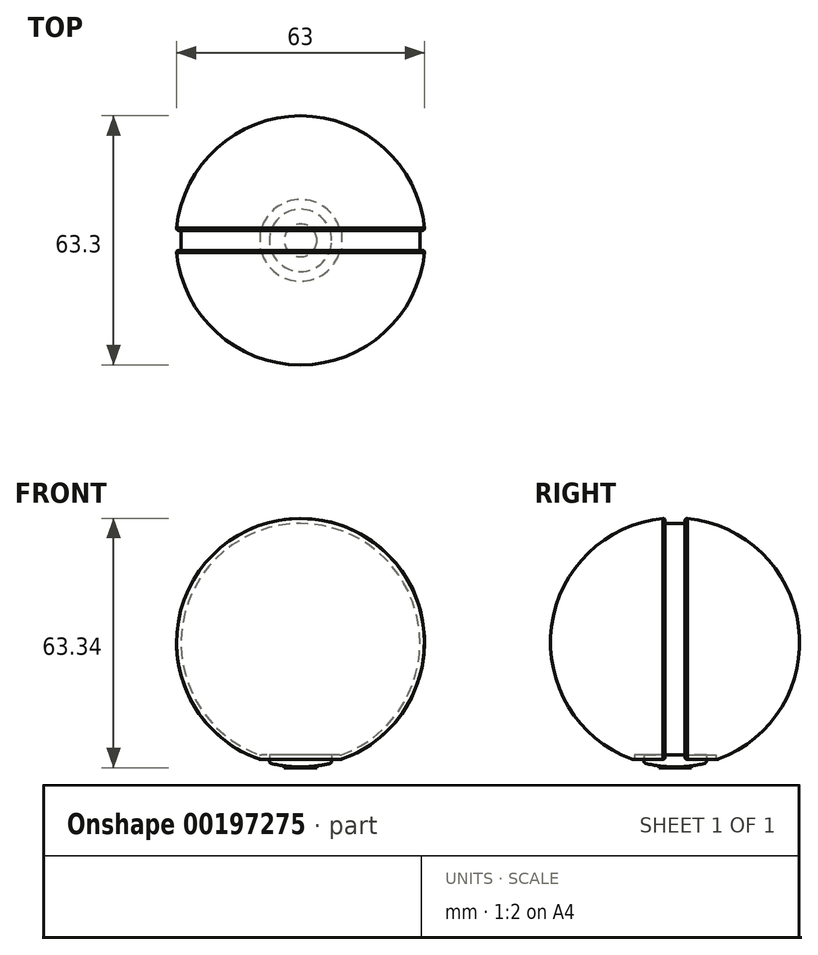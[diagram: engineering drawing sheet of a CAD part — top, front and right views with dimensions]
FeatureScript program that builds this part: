
annotation { "Feature Type Name" : "Feature", "Feature Type Description" : "" }
export const myFeature = defineFeature(function(context is Context, id is Id, definition is map)
    precondition{}
    {
        {
            var Q0;
            Q0=qCreatedBy(makeId("Front.planeOp"),FACE);
            var sketch = newSketch(context, id + "F0", { "sketchPlane" : qUnion([Q0])});
            skLineSegment(sketch, "E0", {"start": v(0, 0) * mm, "end": v(0, 63.3) * mm});
            skArc(sketch, "E1", {"start": v(0, 63.3) * mm, "mid": v(-31.65, 31.65) * mm, "end": v(0, 0) * mm});
            skSolve(sketch);
        }
        {
            var Q0;
            Q0=qSketchRegion(id+"F0",true);
            var Q1;
            Q1=sQuery(id+"F0.wireOp",EDGE,"E0");
            revolve(context, id + "F1", {"entities" : qUnion([Q0]), "axis" : qUnion([Q1]), "revolveType" : RevolveType.FULL});
        }
        {
            var Q0;
            Q0=qCreatedBy(makeId("Front.planeOp"),FACE);
            var sketch = newSketch(context, id + "F2", { "sketchPlane" : qUnion([Q0])});
            skLineSegment(sketch, "E2", {"start": v(10, -3.8) * mm, "end": v(10, 2.88) * mm});
            skLineSegment(sketch, "E3", {"start": v(-10, 2.88) * mm, "end": v(-10, -3.8) * mm});
            skLineSegment(sketch, "E4", {"start": v(0, 0) * mm, "end": v(0, 63.04) * mm, "construction": true});
            skArc(sketch, "E5", {"start": v(10, 2.88) * mm, "mid": v(0, 61.85) * mm, "end": v(-10, 2.88) * mm});
            skArc(sketch, "E6", {"start": v(10, -3.8) * mm, "mid": v(0, 68.23) * mm, "end": v(-10, -3.8) * mm});
            skSolve(sketch);
        }
        {
            var Q0;
            Q0=qSketchRegion(id+"F2",true);
            extrude(context, id + "F3", {"entities" : qUnion([Q0]), "operationType" : NewBodyOperationType.REMOVE, "oppositeDirection" : true, "depth" : 2.54 * mm, "hasSecondDirection" : true, "secondDirectionOppositeDirection" : false, "secondDirectionDepth" : 2.54 * mm});
        }
        {
            var Q0;
            Q0=qSketchRegion(id+"F2",true);
            extrude(context, id + "F4", {"entities" : qUnion([Q0]), "operationType" : NewBodyOperationType.REMOVE, "oppositeDirection" : true, "depth" : 2 * mm, "hasSecondDirection" : true, "secondDirectionOppositeDirection" : false, "secondDirectionDepth" : 2 * mm});
        }
        {
            var Q0;
            Q0=makeQuery(id+"F3.boolean.opBoolean","INTERSECT",EDGE,{"derivedFrom":[makeQuery(id+"F1.opRevolve","SWEPT_FACE",FACE,{"disambiguationData":[OSD([sQuery(id+"F0.wireOp",EDGE,"E1")])]}),makeQuery(id+"F3.opExtrude","CAP_FACE",FACE,{"disambiguationData":[OSD([sQuery(id+"F2.wireOp",EDGE,"E2"),sQuery(id+"F2.wireOp",EDGE,"E3"),sQuery(id+"F2.wireOp",EDGE,"E5"),sQuery(id+"F2.wireOp",EDGE,"E6")])],"isStart":true})]});
            var Q1;
            Q1=makeQuery(id+"F3.boolean.opBoolean","INTERSECT",EDGE,{"derivedFrom":[makeQuery(id+"F1.opRevolve","SWEPT_FACE",FACE,{"disambiguationData":[OSD([sQuery(id+"F0.wireOp",EDGE,"E1")])]}),makeQuery(id+"F3.opExtrude","CAP_FACE",FACE,{"disambiguationData":[OSD([sQuery(id+"F2.wireOp",EDGE,"E2"),sQuery(id+"F2.wireOp",EDGE,"E3"),sQuery(id+"F2.wireOp",EDGE,"E5"),sQuery(id+"F2.wireOp",EDGE,"E6")])],"isStart":false})]});
            fillet(context, id + "F5", {"entities" : qUnion([Q0, Q1]), "radius" : .5 * mm, "tangentPropagation" : true, "allowEdgeOverflow" : false});
        }
        {
            var Q0;
            Q0=makeQuery(id+"F3.boolean.opBoolean","INTERSECT",EDGE,{"derivedFrom":[makeQuery(id+"F1.opRevolve","SWEPT_FACE",FACE,{"disambiguationData":[OSD([sQuery(id+"F0.wireOp",EDGE,"E1")])]}),makeQuery(id+"F3.opExtrude","SWEPT_FACE",FACE,{"disambiguationData":[OSD([sQuery(id+"F2.wireOp",EDGE,"E2")])]})]});
            var Q1;
            Q1=makeQuery(id+"F3.boolean.opBoolean","INTERSECT",EDGE,{"derivedFrom":[makeQuery(id+"F1.opRevolve","SWEPT_FACE",FACE,{"disambiguationData":[OSD([sQuery(id+"F0.wireOp",EDGE,"E1")])]}),makeQuery(id+"F3.opExtrude","SWEPT_FACE",FACE,{"disambiguationData":[OSD([sQuery(id+"F2.wireOp",EDGE,"E3")])]})]});
            fillet(context, id + "F6", {"entities" : qUnion([Q0, Q1]), "radius" : .2 * mm, "tangentPropagation" : true, "allowEdgeOverflow" : false});
        }
        {
            var Q0;
            Q0=qCreatedBy(makeId("Top.planeOp"),FACE);
            var sketch = newSketch(context, id + "F7", { "sketchPlane" : qUnion([Q0])});
            skCircle(sketch, "E7", {"center": v(0, 0) * mm, "radius": 10.36 * mm});
            skCircle(sketch, "E8", {"center": v(0, 0) * mm, "radius": 7.92 * mm});
            skSolve(sketch);
        }
        {
            var Q0;
            Q0=qSketchRegion(id+"F7",true);
            extrude(context, id + "F8", {"entities" : qUnion([Q0]), "operationType" : NewBodyOperationType.REMOVE, "depth" : 3 * mm});
        }
        {
            var Q0;
            Q0=makeQuery(id+"F8.boolean.opBoolean","INTERSECT",EDGE,{"disambiguationData":[OD(0.0)],"derivedFrom":[makeQuery(id+"F1.opRevolve","SWEPT_FACE",FACE,{"disambiguationData":[OSD([sQuery(id+"F0.wireOp",EDGE,"E1")])]}),makeQuery(id+"F8.opExtrude","SWEPT_FACE",FACE,{"disambiguationData":[OSD([sQuery(id+"F7.wireOp",EDGE,"E7")])]})]});
            var Q1;
            Q1=makeQuery(id+"F8.boolean.opBoolean","INTERSECT",EDGE,{"disambiguationData":[OD(1.0)],"derivedFrom":[makeQuery(id+"F1.opRevolve","SWEPT_FACE",FACE,{"disambiguationData":[OSD([sQuery(id+"F0.wireOp",EDGE,"E1")])]}),makeQuery(id+"F8.opExtrude","SWEPT_FACE",FACE,{"disambiguationData":[OSD([sQuery(id+"F7.wireOp",EDGE,"E7")])]})]});
            fillet(context, id + "F9", {"entities" : qUnion([Q0, Q1]), "radius" : .5 * mm, "tangentPropagation" : true, "allowEdgeOverflow" : false});
        }
        {
            var Q0;
            Q0=qCreatedBy(makeId("Top.planeOp"),FACE);
            var sketch = newSketch(context, id + "F10", { "sketchPlane" : qUnion([Q0])});
            skCircle(sketch, "E9", {"center": v(0, 0) * mm, "radius": 4.15 * mm});
            skSolve(sketch);
        }
        {
            var Q0;
            Q0=qSketchRegion(id+"F10",true);
            extrude(context, id + "F11", {"entities" : qUnion([Q0]), "operationType" : NewBodyOperationType.ADD, "oppositeDirection" : true, "depth" : .2 * mm});
        }
        {
            var Q0;
            Q0=makeQuery(id+"F8.boolean.opBoolean","INTERSECT",EDGE,{"derivedFrom":[makeQuery(id+"F1.opRevolve","SWEPT_FACE",FACE,{"disambiguationData":[OSD([sQuery(id+"F0.wireOp",EDGE,"E1")])]}),makeQuery(id+"F8.opExtrude","SWEPT_FACE",FACE,{"disambiguationData":[OSD([sQuery(id+"F7.wireOp",EDGE,"E8")])]})]});
            fillet(context, id + "F12", {"entities" : qUnion([Q0]), "radius" : .5 * mm, "tangentPropagation" : true, "allowEdgeOverflow" : false});
        }
    });
